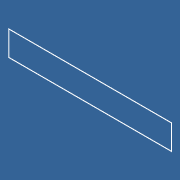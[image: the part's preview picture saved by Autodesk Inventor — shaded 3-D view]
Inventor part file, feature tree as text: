
AUTODESK INVENTOR PART (.ipt)
format: ipt  version: unknown  size: 166,400 bytes
history: native  units: in
note: dims shown in document units (in); Inventor stores cm internally (conversion verified against a paired STEP export)
features: extrude x1, sketch x1
ambient origin geometry x8: Origin, YZ Plane, XZ Plane, XY Plane, X Axis, Y Axis, Z Axis, Center Point
bodies: Solid1 (feature_tree)
feature tree (2):
  extrude  "Extrusion1"  Depth=50.0in
  sketch  "Sketch1"  dims[d0=318.0in d1=50.0in d2=2.0in d3=0.06in d4=0.0in]
